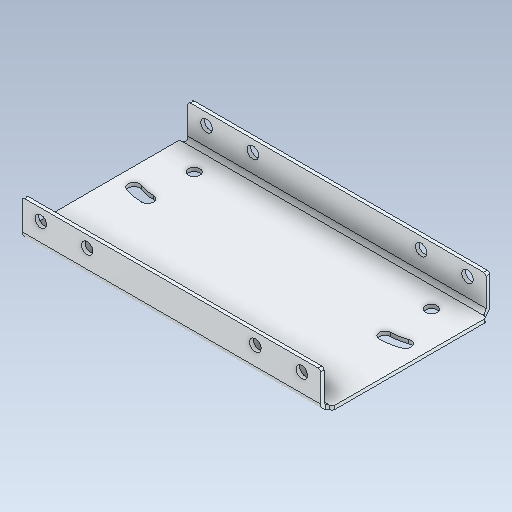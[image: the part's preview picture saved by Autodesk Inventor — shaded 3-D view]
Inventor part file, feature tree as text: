
AUTODESK INVENTOR PART (.ipt)
format: ipt  version: 2021 (Build 250183000, 183)  size: 161,280 bytes
history: native  units: in
note: dims shown in document units (in); Inventor stores cm internally (conversion verified against a paired STEP export)
features: fillet x1
ambient origin geometry x8: Origin, YZ Plane, XZ Plane, XY Plane, X Axis, Y Axis, Z Axis, Center Point
bodies: Solid1 (feature_tree)
feature tree (1):
  fillet  "Fillet1"  [1 undecoded]
note: 1 required parameter value undecoded (feature->parameter linkage not recoverable at this tier; creation-order binding heuristic only, values carry confidence <= 0.55)
